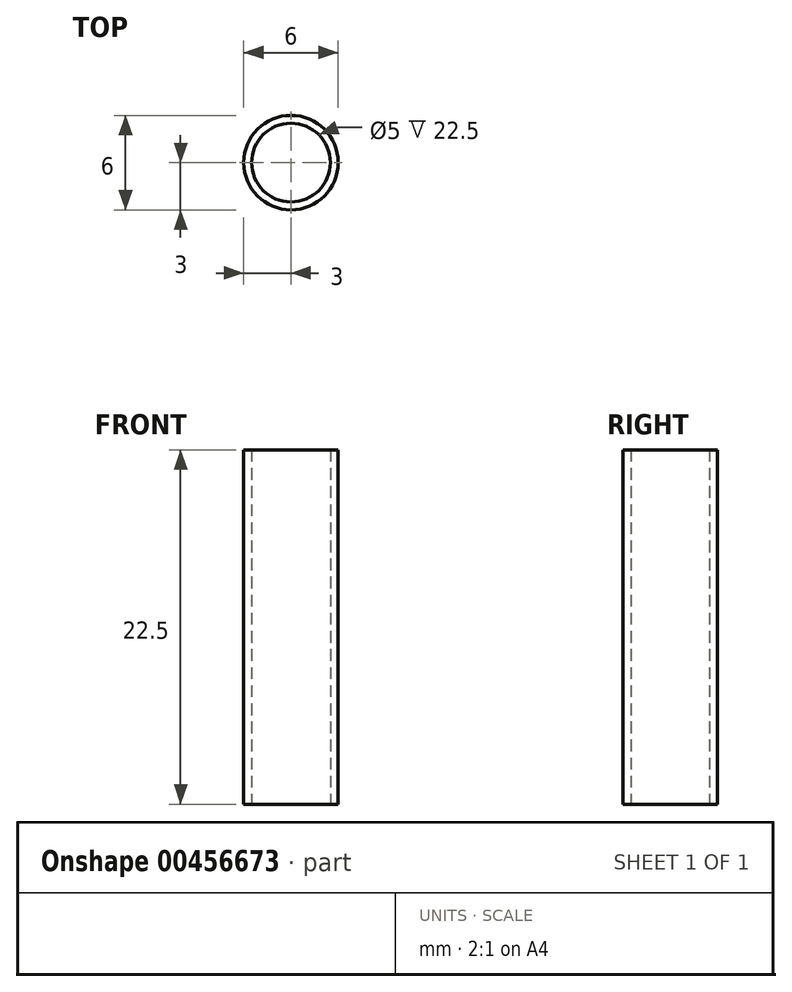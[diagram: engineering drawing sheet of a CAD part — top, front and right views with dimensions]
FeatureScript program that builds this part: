
annotation { "Feature Type Name" : "Feature", "Feature Type Description" : "" }
export const myFeature = defineFeature(function(context is Context, id is Id, definition is map)
    precondition{}
    {
        {
            var Q0;
            Q0=qCreatedBy(makeId("Top.planeOp"),FACE);
            var sketch = newSketch(context, id + "F0", { "sketchPlane" : qUnion([Q0])});
            skCircle(sketch, "E0", {"center": v(0, 0) * mm, "radius": 3 * mm});
            skCircle(sketch, "E1", {"center": v(0, 0) * mm, "radius": 2.5 * mm});
            skSolve(sketch);
        }
        {
            var Q0;
            Q0=makeQuery(id+"F0.imprint","IMPRINT",FACE,{"disambiguationData":[TD([[makeQuery(id+"F0.imprint","IMPRINT",EDGE,{"derivedFrom":sQuery(id+"F0.wireOp",EDGE,"E0")}),1.0]])]});
            extrude(context, id + "F1", {"entities" : qUnion([Q0]), "depth" : 22.5 * mm});
        }
    });
